# Revit family: Cajas fijas Legrand Linkeo con paneles laterales fijos
name_source: partatom
category: Equipement spécialisé
units: mm (PartAtom-declared; Revit-internal decimal feet)

## family parameters
Basée sur le plan de construction = Non
Cote de connecteur circulaire = Utiliser le diamètre
Couper avec des vides une fois chargée = Non
Numéro OmniClass = 23.80.30.11.17
Partagée = Oui
Point de calcul de pièce = Non
Titre OmniClass = Distribution Boards and Control Panels
Toujours verticalement = Oui
Type d'élément = Normal

## types (12) — shared parameters
Acabado del carril de perfil = En forma de L
Anchura (mm) = 605 mm  [stored 1.98491 ft]
Anchura útil (mm) = 526 mm  [stored 1.72572 ft]
Clase de aplicación = Cajas
Clase de protección IK = IK08
Clase de protección IP = IP20
Color = gris
Con conexión a tierra = Oui
Con paredes laterales = Oui
Con puerta frontal = Oui
Con techo en chapa = Oui
Desmontable = Oui
E-catalogo enlace = https://www.legrand.fr
Espesor (mm) = 1.5 mm  [stored 0.00492126 ft]
Fabricant = Legrand
Función = Cajas fijas Linkeo Legrand
Material = Acero
Modelo = Estructura fija
Numero RAL = 7016
Número de puertas = 1
Sujeción X = 400 mm  [stored 1.31234 ft]
Tamaño modular = 482.6 mm (19 pulgadas)
Tipo de montaje = Frontal
Tipo de ventilación = Pasivo
Tratamiento de superficie = Recubrimiento con polvo
Ubicación del rack = 40 mm
zero-valued in all types: Elévation par défaut

## per-type parameters (varying)
| type | Altura (mm) | Altura útil (mm) | EAN | Máxima capacidad de carga | Módulos de altura | Número de pieza Legrand | Profundidad (mm) | Sujeción Y |
| Caja fija Legrand Linkeo con paneles laterales fijos 12U W600 D450 646202.rfa | 625 mm | 555 mm | 3414970967794 | 36 | 12 | 646202 | 454 mm  [stored 1.4895 ft] | 419 mm |
| Caja fija Legrand Linkeo con paneles laterales fijos 12U W600 D600 646212.rfa | 625 mm | 555 mm | 3414970967855 | 36 | 12 | 646212 | 604 mm | 419 mm |
| Caja fija Legrand Linkeo con paneles laterales fijos 15U W600 D450 646203.rfa | 759 mm | 688 mm | 3414970967800 | 45 | 15 | 646203 | 454 mm  [stored 1.4895 ft] | 552 mm |
| Caja fija Legrand Linkeo con paneles laterales fijos 15U W600 D600 646213.rfa | 759 mm | 688 mm | 3414970967862 | 45 | 15 | 646213 | 604 mm | 552 mm |
| Caja fija Legrand Linkeo con paneles laterales fijos 18U W600 D450 646204.rfa | 892 mm  [stored 2.92651 ft] | 821 mm  [stored 2.69357 ft] | 3414970967817 | 54 | 18 | 646204 | 454 mm  [stored 1.4895 ft] | 685 mm  [stored 2.24738 ft] |
| Caja fija Legrand Linkeo con paneles laterales fijos 18U W600 D600 646214.rfa | 892 mm  [stored 2.92651 ft] | 821 mm  [stored 2.69357 ft] | 3414970967879 | 54 | 18 | 646214 | 604 mm | 685 mm  [stored 2.24738 ft] |
| Caja fija Legrand Linkeo con paneles laterales fijos 21U W600 D450 646205.rfa | 1025 mm | 955 mm | 3414970967824 | 63 | 21 | 646205 | 454 mm  [stored 1.4895 ft] | 819 mm |
| Caja fija Legrand Linkeo con paneles laterales fijos 21U W600 D600 646215.rfa | 1025 mm | 955 mm | 3414970967886 | 63 | 21 | 646215 | 604 mm | 819 mm |
| Caja fija Legrand Linkeo con paneles laterales fijos 6U W600 D450 646200.rfa | 359 mm | 288 mm | 3414970967770 | 18 | 6 | 646200 | 454 mm  [stored 1.4895 ft] | 152 mm |
| Caja fija Legrand Linkeo con paneles laterales fijos 6U W600 D600 646210.rfa | 359 mm | 288 mm | 3414970967831 | 18 | 6 | 646210 | 604 mm | 152 mm |
| Caja fija Legrand Linkeo con paneles laterales fijos 9U W600 D450 646201.rfa | 492 mm | 422 mm | 3414970967787 | 27 | 9 | 646201 | 454 mm  [stored 1.4895 ft] | 286 mm |
| Caja fija Legrand Linkeo con paneles laterales fijos 9U W600 D600 646211.rfa | 492 mm | 422 mm | 3414970967848 | 27 | 9 | 646211 | 604 mm | 286 mm |

note: column(s) folded — value = type name in every type: Formulación BIM

note: [stored X ft] marks values corroborated as IEEE doubles in the binary element streams (Revit-internal decimal feet)
